# Revit family: agtatec_Record_RlvngDrsetSym_K31_WallBased
name_source: partatom
category: Doors
revit_build: Autodesk Revit Architecture 2012 (Build: 20110916_2132(x64)
units: mm (PartAtom-declared; Revit-internal decimal feet)

## types (2) — shared parameters
AccessoryOptions = Contact manufacturer
AlternativeDoorsetGlazing = Part of glazing spec
AntiFingerTrapRequirement = Yes
Assembly Code = B2030300
BIMObjectName = agtatec_Record_RevolvingDoorsetSystem_K31_WallBased
BottomConstruction = agtatec_Record_Revolving Door, Stainless Steel
CanopyCovering = agtatec_Record_Revolving Door, Sheet metal (Painted Steel)
CanopyHeight = 350 mm  [stored 1.14829 ft]
CanopyHeightOptions = 250 mm +
Capacity = <>
Colour = Customer specific
Configuration = 2, 3 or 4 leafs
Construction Type = Automatic Revolving Door
DepthOfRecessFloorFrame = 80 mm  [stored 0.262467 ft]
Description = 3-wing Revolving Door
DiameterOptions = Internal 2000-4000 mm
DoorIncluded = Yes
DoorLeafCollapse = No
DoorLeafsAngle = 121.00°
DoorSeal = 1
DoorWingOptions = 3 wings
DoorsetFasteners = Screws
DoorsetOperation = Automatic
DoorsetOptions = Ridig, Sliding door, Display case
DrumWallPanelFill = agtatec_Record_Revolving Door, Laminated Safety Glass (Clear)
DurationUnit = year
ElectronicLock = Yes
ExternalDimensionOfFloorFrame = 3554 mm  [stored 11.6601 ft]
Finish = Powder coated, Anodized, customer specific
FireExit = No
FloorFrame(Ring) = Yes
Flooring = agtatec_Record_Revolving Door, Felt Carpet
FrameMaterial = Aluminium
FrameProfile = Aluminium
FrameSeal = Yes
Function = Exterior
GlassLayers = 1
GlassThickness1 = <>
GlassThickness2 = None (default)
GlassType = Part of glazing spec
HandicapAccessible = No
Handles = Yes
HasDrive = Yes
Height = 2550 mm  [stored 8.36614 ft]
HeightOfFloorFrame = 65 mm  [stored 0.213255 ft]
HeightUnderCanopyOptions = Passage height: 2000 - 3000 mm
IfcExportAs = IfcDoorStyle
IfcExportType = Door
InsideDiameter = 3302 mm
IsExternal = Yes
IssueDate = <>
LeafColourOptions = All RAL, customer specific
LeafPanelFill = agtatec_Record_Revolving Door, Laminated Safety Glass (Clear)
LeafRotationAngle = 0.00°
ManufacturerName = Record
ManufacturerURL = www.agta-record.com
Material = Aluminium
Model = K31
ModelReference = Depends on the configuration
NBSDescription = Revolving Doorset System
NBSReference = 25-50-20/170
Name = RlvngDrsetSym_K31_WallBased_Record
NightShutterPanelFill = agtatec_Record_Revolving Door, Laminated Safety Glass (Clear)
NightShuttersOpen = Yes
NominalHeight = 2550 mm  [stored 8.36614 ft]
NominalLength = 3360 mm  [stored 11.0236 ft]
NominalWidth = 3360 mm  [stored 11.0236 ft]
OperatingTemperature = -15º to +50ºC
OutsideDiameter = 3354 mm  [stored 11.0039 ft]
PanelFrames = agtatec_Record_Revolving Door, Aluminium
PassageHeight = 2200 mm  [stored 7.21785 ft]
PassageWidth = 1550 mm  [stored 5.0853 ft]
ProductInformation = www.agta-record.com
RecessHeight = 2600 mm  [stored 8.53018 ft]
RecessWidth = 3460 mm  [stored 11.3517 ft]
ReferenceStandard = EN16005, EN16361, DIN 18650, etc.
ReplacementCost = Depends on the configuration and door type
Rough Height = 2556 mm
Rough Width = 3366 mm
SafetyDevices = Fully compliant with EN16005, Safety buffers, Presence sensors, etc.
SelfClosing = Yes
ServiceLifeDuration = 10-15 years
Shape = Cylinder shaped
SmokeStop = No
ThresholdRequired = Yes
ThresholdStripping = No additional required, part of the doorset
TotalDiameter = 3360 mm  [stored 11.0236 ft]
TotalHeight = 2550 mm  [stored 8.36614 ft]
URL = www.agta-record.com
Uniclass2 = Ss_25_30_20_70
Version = Version 1.0
WarrantyDescription = Depends on country
WarrantyDurationLabour = Depends on country
WarrantyDurationParts = Depends on country
WarrantyDurationUnit = Depends on country
WarrantyGuarantorLabour = Local door manufacturer
WarrantyGuarantorParts = Local door manufacturer
Weight = Depends on configuration and size
Width = 3360 mm  [stored 11.0236 ft]
WithinStandardSizes = Yes
zero-valued in all types: Cost, OffsetFromWallCenter, OffsetFromWallSide, OffsetFromWallTop, ThermalTransmittance

## type names (no varying parameters)
- Default
- default

note: [stored X ft] marks values corroborated as IEEE doubles in the binary element streams (Revit-internal decimal feet)

## geometry (parser evidence)
native form markers: Sweep x14
no freeform markers — native parametric forms only
